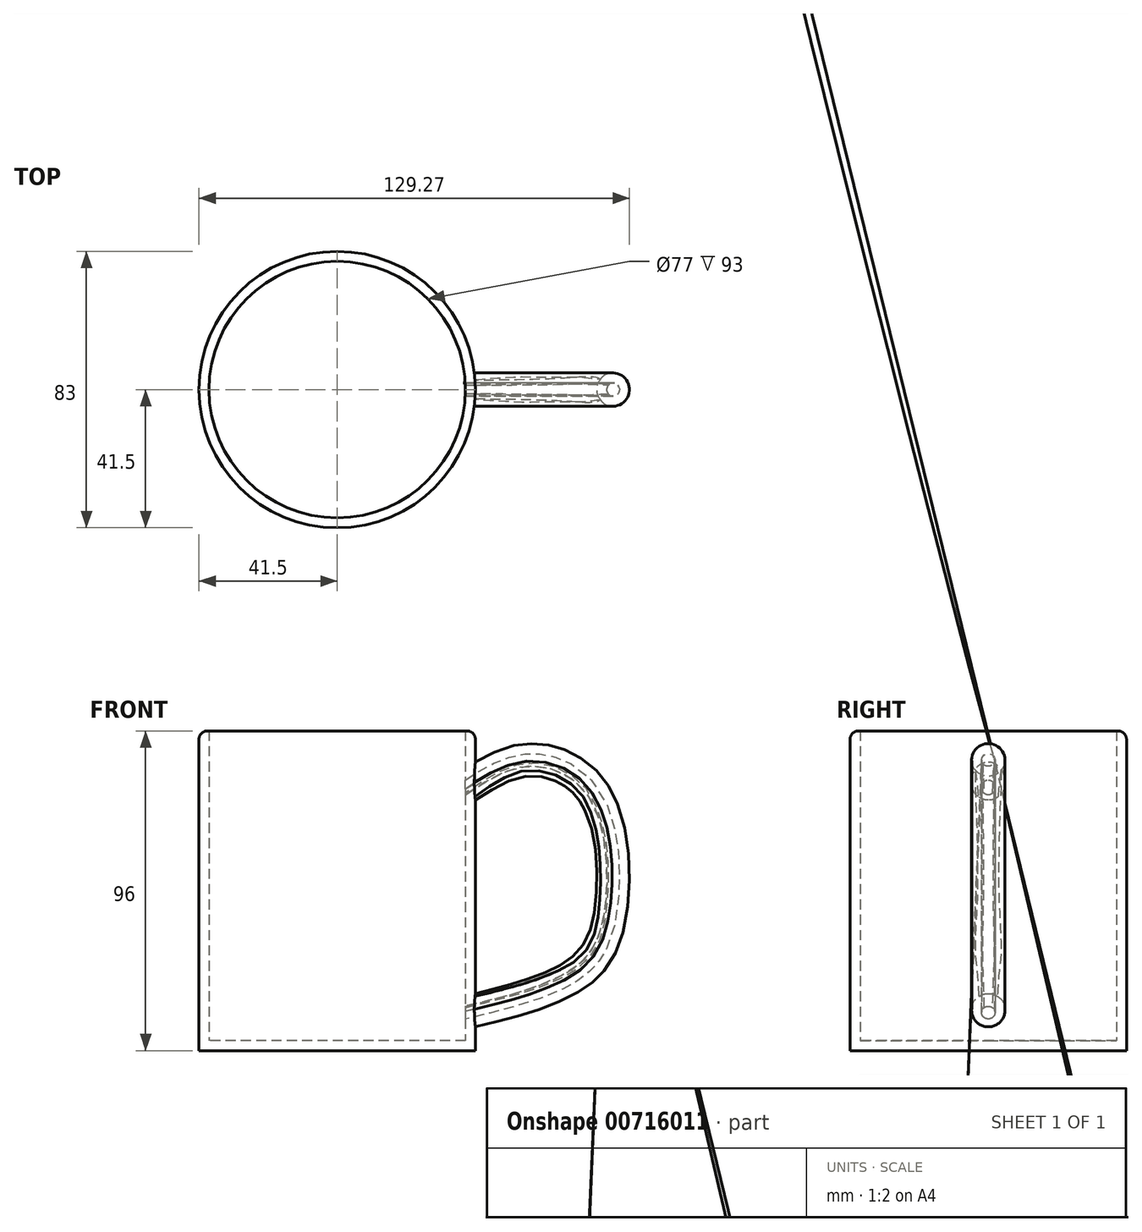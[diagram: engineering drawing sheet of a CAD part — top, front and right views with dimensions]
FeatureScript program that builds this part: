
annotation { "Feature Type Name" : "Feature", "Feature Type Description" : "" }
export const myFeature = defineFeature(function(context is Context, id is Id, definition is map)
    precondition{}
    {
        {
            var Q0;
            Q0=qCreatedBy(makeId("Top.planeOp"),FACE);
            var sketch = newSketch(context, id + "F0", { "sketchPlane" : qUnion([Q0])});
            skCircle(sketch, "E0", {"center": v(0, 0) * mm, "radius": 41.5 * mm});
            skSolve(sketch);
        }
        {
            var Q0;
            Q0=makeQuery(id+"F0.imprint","IMPRINT",FACE,{"disambiguationData":[TD([[makeQuery(id+"F0.imprint","IMPRINT",EDGE,{"derivedFrom":sQuery(id+"F0.wireOp",EDGE,"E0")}),1.0]])]});
            extrude(context, id + "F1", {"entities" : qUnion([Q0]), "depth" : 96 * mm, "offsetDistance" : 25 * mm});
        }
        {
            var Q0;
            Q0=qCreatedBy(makeId("Front.planeOp"),FACE);
            var sketch = newSketch(context, id + "F2", { "sketchPlane" : qUnion([Q0])});
            skFitSpline(sketch, "E1", {"points": [v(36.14, 77.76) * mm, v(57.2, 87.52) * mm, v(77.24, 77.5) * mm, v(82.63, 43.35) * mm, v(73.38, 23.83) * mm, v(36.66, 10.73) * mm], "startDerivative": vector(111.4, 75.67) * mm, "endDerivative": vector(-182.06, -43.06) * mm});
            skSolve(sketch);
        }
        {
            var Q0;
            Q0=qCreatedBy(makeId("Right.planeOp"),FACE);
            cPlane(context, id + "F3", {"entities" : qUnion([Q0]), "cplaneType" : CPlaneType.OFFSET, "offset" : 37.2 * mm, "width" : 150 * mm, "height" : 150 * mm});
        }
        {
            var Q0;
            Q0=qCreatedBy(id+"F3.planeOp",FACE);
            var sketch = newSketch(context, id + "F4", { "sketchPlane" : qUnion([Q0])});
            skCircle(sketch, "E2", {"center": v(0, 77.42) * mm, "radius": 5 * mm});
            skCircle(sketch, "E3", {"center": v(0, 11.12) * mm, "radius": 5 * mm});
            skSolve(sketch);
        }
        {
            var Q0;
            Q0 = qSketchRegion(id + "F4", true);
            var Q1;
            Q1=sQuery(id+"F2.wireOp",EDGE,"E1");
            sweep(context, id + "F5", {"operationType" : NewBodyOperationType.ADD, "profiles" : qUnion([Q0]), "path" : qUnion([Q1])});
        }
        {
            var Q0;
            Q0=makeQuery(id+"F1.opExtrude","CAP_FACE",FACE,{"disambiguationData":[OSD([sQuery(id+"F0.wireOp",EDGE,"E0")])],"isStart":false});
            shell(context, id + "F6", {"entities" : qUnion([Q0]), "thickness" : 3 * mm});
        }
        {
            var Q0;
            Q0=makeQuery(id+"F1.opExtrude","CAP_EDGE",EDGE,{"disambiguationData":[OSD([sQuery(id+"F0.wireOp",EDGE,"E0")])],"isStart":false});
            fillet(context, id + "F7", {"entities" : qUnion([Q0]), "radius" : 2.5 * mm, "tangentPropagation" : true, "allowEdgeOverflow" : false});
        }
    });
